# Revit family: TW Mischventil 7766 51
name_source: partatom
category: Rohrzubehör
units: mm (PartAtom-declared; Revit-internal decimal feet)

## family parameters
Arbeitsebenenbasiert = Nein
Beim Laden mit Abzugskörper schneiden = Nein
Bemaßung runder Anschluss = Durchmesser verwenden
Gemeinsam genutzt = Nein
Immer vertikal = Ja
OmniClass-Nummer = 23.65.55.14
OmniClass-Titel = Valves for Liquid Services
Teiletyp = Unterbricht

## types (1)
- TW Mischventil 7766 51
    Anschlussgewinde = flachdichtend, G 3/4
    Arbeitsdruck (statisch) = 1000000.0 Pa
    Bestellnummer = 2776651
    Dichtung = EPDM
    Durchfluss bei 3 bar = 0.4 L/s
    Feder = Edelstahl 1.4310
    Funktion = Das thermostatische Mischventil 7766 TMV wird in Anlagen mit erwärmten Trinkwasser eingesetzt.
Unabhängig von Druck- oder Temperaturänderungen des im Ventil zu vermischenden Kalt- und Warmwassers, wird das gemischte Wasser konstant auf den voreingestellten Temperatur- und Durchflusswert geregelt.
Das Thermostatventil arbeitet vollkommen selbstständig und ohne Hilfsenergie.
Der nach der Installation einmal voreingestellte Wert der gewünschten Mischtemperatur, wird innerhalb einer regeltechnischen Hysterese konstant gehalten.
    Gehäuse = entzinkungsbeständiges Messing CC770S
    H01 = 44 mm  [stored 0.144357 ft]
    H02 = 19 mm  [stored 0.062336 ft]
    H03 = 40 mm  [stored 0.131234 ft]
    H04 = 2 mm  [stored 0.00656168 ft]
    H05 = 12 mm  [stored 0.0393701 ft]
    H06 = 58 mm  [stored 0.190289 ft]
    Handrad = ABS
    Hersteller = HERZ Armaturen Ges.m.b.H.
    Hinweis = Gemäß Art 33 der REACH-Verordnung (EG Nr. 1907/2006) sind wir verpflichtet, darauf hinzuweisen, dass der Stoff Blei auf der SVHC-Liste geführt wird und dass alle aus Messing bestehenden Bauteile, die in unseren Erzeugnissen verarbeitet sind, mehr als 0,1 % (w/w) Blei (CAS: 7439-92-1 / EINECS: 231-100-4) enthalten.
Da Blei als Legierungsbestandteil fest gebunden ist, sind keine Expositionen zu erwarten und daher sind keine zusätzlichen Angaben zur sicheren Verwendung notwendig.
    Innenteil = entzinkungsbeständiges Messing CW626N
    L01 = 32 mm  [stored 0.104987 ft]
    L02 = 12 mm  [stored 0.0393701 ft]
    L03 = 7 mm  [stored 0.0229659 ft]
    L04 = 5 mm  [stored 0.0164042 ft]
    L05 = 8 mm  [stored 0.0262467 ft]
    Max. Arbeitsdruck (dynamisch) = 0.2 - 6 bar
    Max. Betriebstemp. WW = 85 °C
    Medium = Trinkwasser
    Min. Betriebstemp. KW = 5 °C - 25 °C
    Min. Durchfluss = 0.1 L/s
    Min. Übertemp. HW-WW = 15 °C
    Mischtemp. (Werkseinstellung) = 38 °C
    Nennweite = 20 mm  [stored 0.0656168 ft]
    R01 = 10 mm  [stored 0.0328084 ft]
    R02 = 7 mm  [stored 0.0229659 ft]
    R03 = 9 mm  [stored 0.0295276 ft]
    R04 = 12 mm  [stored 0.0393701 ft]
    R05 = 13 mm
    R06 = 14 mm  [stored 0.0459318 ft]
    R07 = 11 mm  [stored 0.0360892 ft]
    R08 = 15 mm
    R09 = 21 mm
    R10 = 20 mm  [stored 0.0656168 ft]
    R100 = 2 mm  [stored 0.00656168 ft]
    R11 = 18 mm  [stored 0.0590551 ft]
    R12 = 19 mm  [stored 0.062336 ft]
    R13 = 4 mm  [stored 0.0131234 ft]
    R14 = 2 mm  [stored 0.00656168 ft]
    R99 = 1 mm  [stored 0.00328084 ft]
    S01 = 28 mm
    S02 = 41 mm
    SCTWCODE = 04;18;03
    SCTWSEQ = AW;SBT_TYP_AW="104";3
    Sicherheitshinweis = Die verwendete Armatur ist eine SICHERHEITSARMATUR. Ein Austausch spätestens alle 5 Jahre wird empfohlen.
Nationale und regionale Normen, sowie Richtlinien sind zu beachten.
    Spindel = entzinkungsbeständiges Messing CW626N
    Temp. Einstellbereich = 38 °C - 48 °C
    Temperaturstabilität am Ausgang = +-2°C
    URL = www.herz-armaturen.at
    Vorgabe-Ansicht = 0 mm  [stored 0 ft]
    Warnhinweis = • Es wird empfohlen das Ventil mindestens einmal im Jahr zu überprüfen. Bei schlechter oder unbekannter Wassergüte
ist die Prüfung entsprechend öfter durchzuführen.
• Die Prüfung der Auslauftemperatur ist wie bei der Neuinstallation durchzuführen und darf nicht mehr als 2 °C vom
Ersteinstellwert abweichen.
• Die Rückschlagventile sind zur Reinigung leicht zugänglich. Wir empfehlen die Verwendung einer Spitzzange um die
Rückschlagventile aus dem Ventilgehäuse zu ziehen. Aushebeln kann zu Beschädigungen führen.
• Außer der Abnahme des Handrades und der Reinigung der Rückschlagventile ist ein weiteres Zerlegen des Ventils
für Wartungszwecke nicht vorgesehen

note: [stored X ft] marks values corroborated as IEEE doubles in the binary element streams (Revit-internal decimal feet)
